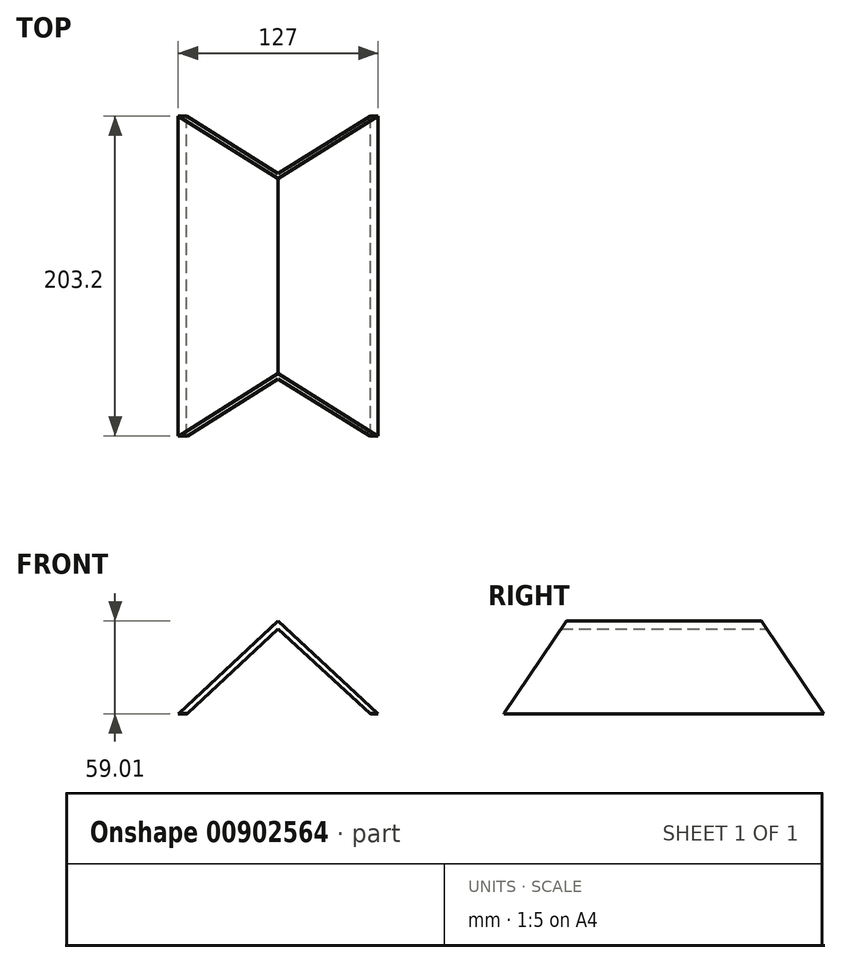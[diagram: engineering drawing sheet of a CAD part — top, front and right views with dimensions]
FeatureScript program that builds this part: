
annotation { "Feature Type Name" : "Feature", "Feature Type Description" : "" }
export const myFeature = defineFeature(function(context is Context, id is Id, definition is map)
    precondition{}
    {
        {
            var Q0;
            Q0=qCreatedBy(makeId("Front.planeOp"),FACE);
            var sketch = newSketch(context, id + "F0", { "sketchPlane" : qUnion([Q0])});
            skLineSegment(sketch, "E0", {"start": v(0, 50.8) * mm, "end": v(-63.5, -8.2) * mm});
            skLineSegment(sketch, "E1", {"start": v(-63.5, -8.2) * mm, "end": v(-58.03, -8.2) * mm});
            skLineSegment(sketch, "E2", {"start": v(63.5, -8.2) * mm, "end": v(0, 50.8) * mm});
            skLineSegment(sketch, "E3", {"start": v(0, 45.72) * mm, "end": v(-58.03, -8.2) * mm});
            skLineSegment(sketch, "E4", {"start": v(0, 45.72) * mm, "end": v(58.8, -8.2) * mm});
            skLineSegment(sketch, "E5.trimOffspring", {"start": v(58.8, -8.2) * mm, "end": v(63.5, -8.2) * mm});
            skSolve(sketch);
        }
        {
            var Q0;
            Q0 = qSketchRegion(id + "F0", true);
            extrude(context, id + "F1", {"entities" : qUnion([Q0]), "depth" : 203.2 * mm, "offsetDistance" : 25.4 * mm});
        }
        {
            var Q0;
            Q0=qCreatedBy(makeId("Right.planeOp"),FACE);
            var sketch = newSketch(context, id + "F2", { "sketchPlane" : qUnion([Q0])});
            skLineSegment(sketch, "E6", {"start": v(0, 51.23) * mm, "end": v(0, -8.2) * mm});
            skLineSegment(sketch, "E7", {"start": v(0, -8.2) * mm, "end": v(-40.1, 51.23) * mm});
            skLineSegment(sketch, "E8", {"start": v(-40.1, 51.23) * mm, "end": v(0, 51.23) * mm});
            skSolve(sketch);
        }
        {
            var Q0;
            Q0 = qSketchRegion(id + "F2", true);
            extrude(context, id + "F3", {"entities" : qUnion([Q0]), "operationType" : NewBodyOperationType.REMOVE, "oppositeDirection" : true, "depth" : 124.97 * mm, "offsetDistance" : 25.4 * mm, "hasSecondDirection" : true, "secondDirectionOppositeDirection" : false, "secondDirectionDepth" : 110.49 * mm});
        }
        {
            var Q0;
            Q0=qCreatedBy(makeId("Right.planeOp"),FACE);
            var sketch = newSketch(context, id + "F4", { "sketchPlane" : qUnion([Q0])});
            skLineSegment(sketch, "E9", {"start": v(-203.48, -8.2) * mm, "end": v(-203.48, 51.23) * mm});
            skLineSegment(sketch, "E10", {"start": v(-203.48, 51.23) * mm, "end": v(-163.39, 51.23) * mm});
            skLineSegment(sketch, "E11", {"start": v(-163.39, 51.23) * mm, "end": v(-203.48, -8.2) * mm});
            skSolve(sketch);
        }
        {
            var Q0;
            Q0 = qSketchRegion(id + "F4", true);
            extrude(context, id + "F5", {"entities" : qUnion([Q0]), "operationType" : NewBodyOperationType.REMOVE, "oppositeDirection" : true, "depth" : 83.57 * mm, "offsetDistance" : 25.4 * mm, "hasSecondDirection" : true, "secondDirectionOppositeDirection" : false, "secondDirectionDepth" : 103.12 * mm});
        }
    });
